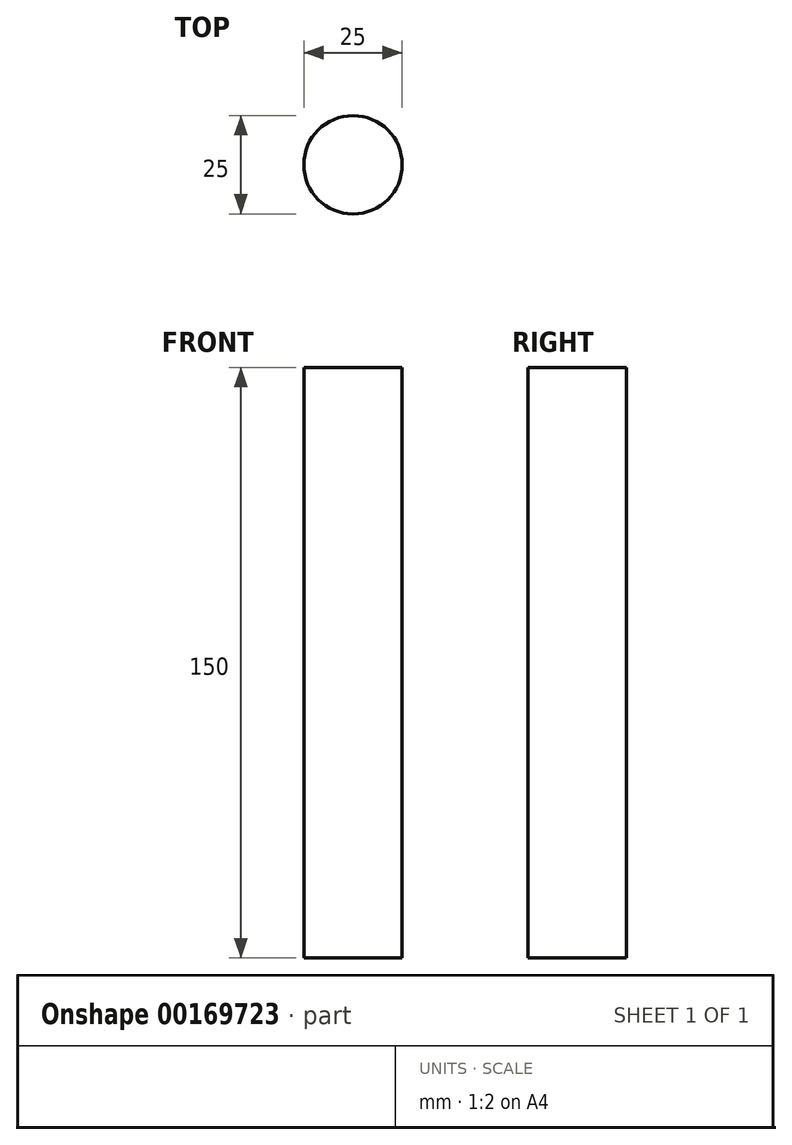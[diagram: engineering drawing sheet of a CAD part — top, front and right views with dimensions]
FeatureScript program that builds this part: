
annotation { "Feature Type Name" : "Feature", "Feature Type Description" : "" }
export const myFeature = defineFeature(function(context is Context, id is Id, definition is map)
    precondition{}
    {
        {
            var Q0;
            Q0=qCreatedBy(makeId("Top.planeOp"),FACE);
            var sketch = newSketch(context, id + "F0", { "sketchPlane" : qUnion([Q0])});
            skCircle(sketch, "E0", {"center": v(0, 0) * mm, "radius": 12.5 * mm});
            skSolve(sketch);
        }
        {
            var Q0;
            Q0=qSketchRegion(id+"F0",true);
            extrude(context, id + "F1", {"entities" : qUnion([Q0]), "depth" : 150 * mm});
        }
    });
